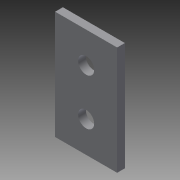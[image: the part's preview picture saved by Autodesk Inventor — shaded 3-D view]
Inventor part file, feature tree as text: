
AUTODESK INVENTOR PART (.ipt)
format: ipt  version: 2013 (Build 170138000, 138)  size: 76,288 bytes
history: native  units: in
note: dims shown in document units (in); Inventor stores cm internally (conversion verified against a paired STEP export)
features: extrude x1, sketch x1
ambient origin geometry x8: Origin, YZ Plane, XZ Plane, XY Plane, X Axis, Y Axis, Z Axis, Center Point
bodies: Solid1 (feature_tree)
feature tree (2):
  extrude  "Extrusion1"  Depth=1.75in
  sketch  "Sketch1"  dims[d0=1.0in d2=1.75in d3=0.26in d4=0.75in d5=0.5in d6=0.125in d7=0.0in]
